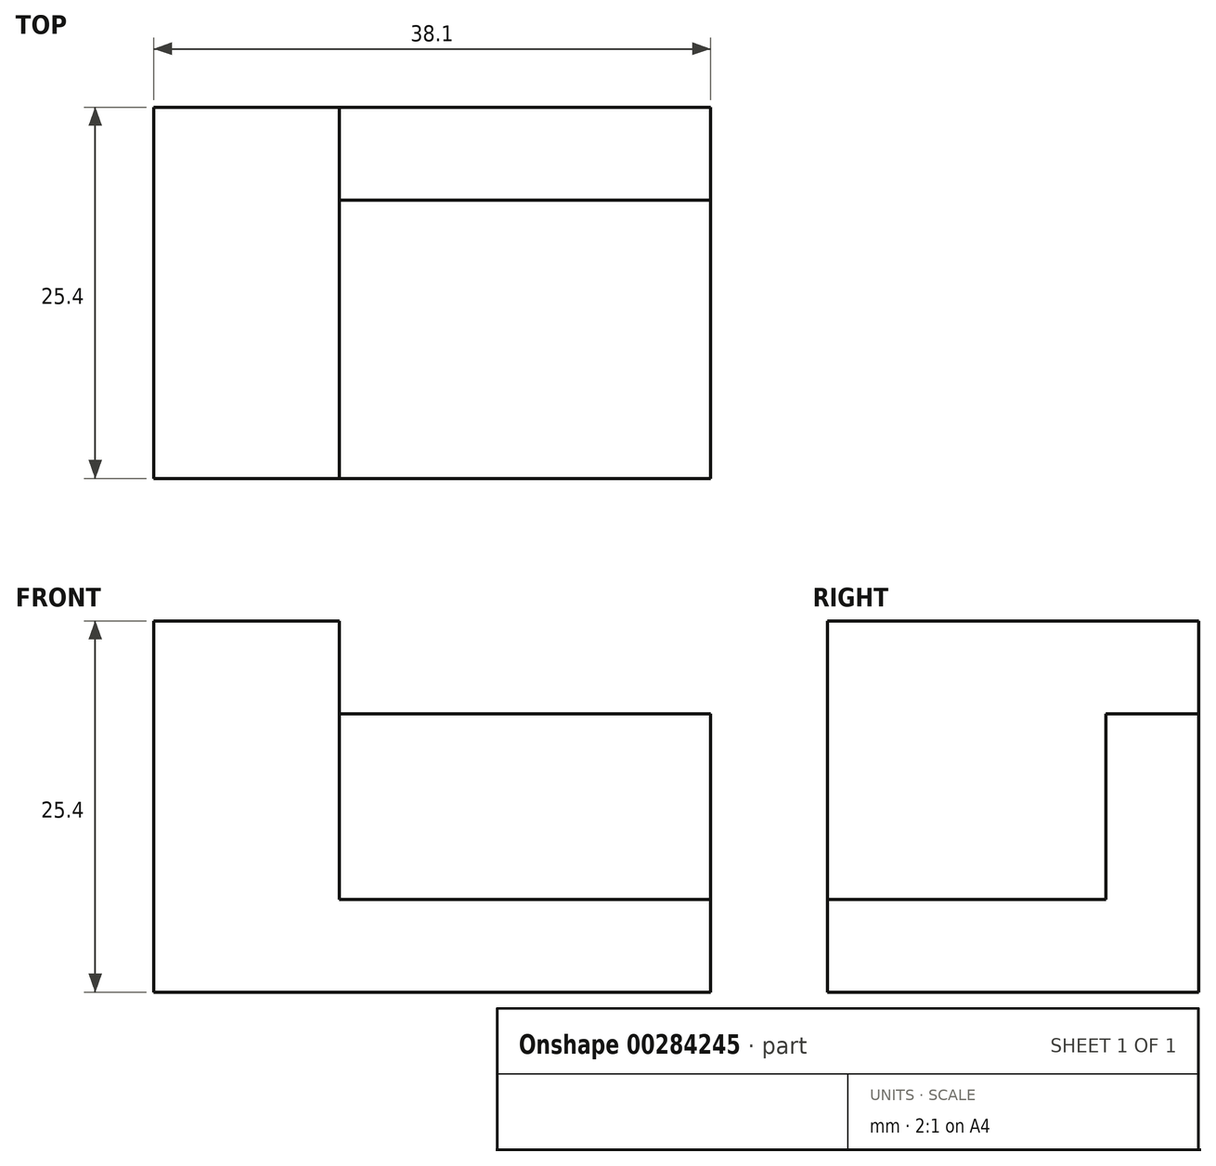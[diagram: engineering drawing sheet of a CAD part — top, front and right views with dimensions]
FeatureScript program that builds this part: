
annotation { "Feature Type Name" : "Feature", "Feature Type Description" : "" }
export const myFeature = defineFeature(function(context is Context, id is Id, definition is map)
    precondition{}
    {
        {
            var Q0;
            Q0=qCreatedBy(makeId("Front.planeOp"),FACE);
            var sketch = newSketch(context, id + "F0", { "sketchPlane" : qUnion([Q0])});
            skLineSegment(sketch, "E0.bottom", {"start": v(0, 0) * mm, "end": v(-12.7, 0) * mm});
            skLineSegment(sketch, "E0.top", {"start": v(0, 25.4) * mm, "end": v(-12.7, 25.4) * mm});
            skLineSegment(sketch, "E0.left", {"start": v(0, 0) * mm, "end": v(0, 25.4) * mm});
            skLineSegment(sketch, "E0.right", {"start": v(-12.7, 0) * mm, "end": v(-12.7, 25.4) * mm});
            skLineSegment(sketch, "E1.bottom", {"start": v(0, 0) * mm, "end": v(25.4, 0) * mm});
            skLineSegment(sketch, "E1.top", {"start": v(0, 6.35) * mm, "end": v(25.4, 6.35) * mm});
            skLineSegment(sketch, "E1.left", {"start": v(0, 0) * mm, "end": v(0, 6.35) * mm});
            skLineSegment(sketch, "E1.right", {"start": v(25.4, 0) * mm, "end": v(25.4, 6.35) * mm});
            skSolve(sketch);
        }
        {
            var Q0;
            Q0 = qSketchRegion(id + "F0", true);
            extrude(context, id + "F1", {"entities" : qUnion([Q0]), "depth" : 25.4 * mm});
        }
        {
            var Q0;
            Q0=qCreatedBy(makeId("Right.planeOp"),FACE);
            var sketch = newSketch(context, id + "F2", { "sketchPlane" : qUnion([Q0])});
            skLineSegment(sketch, "E2.bottom", {"start": v(0, 0) * mm, "end": v(-6.35, 0) * mm});
            skLineSegment(sketch, "E2.top", {"start": v(0, 19.05) * mm, "end": v(-6.35, 19.05) * mm});
            skLineSegment(sketch, "E2.left", {"start": v(0, 0) * mm, "end": v(0, 19.05) * mm});
            skLineSegment(sketch, "E2.right", {"start": v(-6.35, 0) * mm, "end": v(-6.35, 19.05) * mm});
            skSolve(sketch);
        }
        {
            var Q0;
            Q0 = qSketchRegion(id + "F2", true);
            extrude(context, id + "F3", {"entities" : qUnion([Q0]), "operationType" : NewBodyOperationType.ADD, "depth" : 25.4 * mm});
        }
    });
